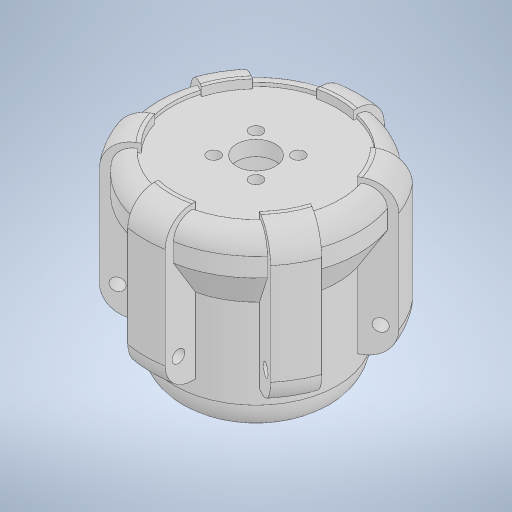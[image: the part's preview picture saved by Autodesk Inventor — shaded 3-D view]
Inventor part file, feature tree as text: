
AUTODESK INVENTOR PART (.ipt)
format: ipt  version: 2024.3 (Build 283343000, 343)  size: 502,272 bytes
history: native  units: mm
features: sketch x7, extrude x3, fillet x3, pattern_circular x3, plane x2, hole x2, projected_geometry x2, revolve x1
ambient origin geometry x8: Origin, YZ Plane, XZ Plane, XY Plane, X Axis, Y Axis, Z Axis, Center Point
bodies: Solid2 (feature_tree)
feature tree (23):
  revolve  "Revolution2"  [1 undecoded]
  plane  "Work Plane1"
  extrude  "Extrusion1"  Depth=10.0mm
  plane  "Work Plane2"
  sketch  "Sketch7"  dims[d18=3.25mm]
  fillet  "Fillet2"  Radius=55.0mm
  pattern_circular  "Circular Pattern1"  [2 undecoded]
  fillet  "Fillet3"  Radius=7.0mm
  hole  "Hole2"  [1 undecoded]
  extrude  "Extrusión3"  Depth=7.0mm
  fillet  "Empalme4"  Radius=8.0mm
  pattern_circular  "Patrón circular2"  [2 undecoded]
  extrude  "Extrusión4"  Depth=7.0mm
  hole  "Agujero3"  [1 undecoded]
  pattern_circular  "Patrón circular3"  [2 undecoded]
  sketch  "Sketch4"  dims[d11=36.85mm d12=10.4mm]
  sketch  "Sketch5"  dims[d13=5.0mm d14=10.0mm d15=55.0mm]
  sketch  "Sketch8"  dims[d19=10.0mm]
  sketch  "Boceto10"  dims[d22=43.425mm]
  projected_geometry  "Contorno proyectado2"
  sketch  "Boceto11"  dims[d24=90.0deg]
  projected_geometry  "Contorno proyectado3"
  sketch  "Boceto12"  dims[d25=-24.682mm d29=15.0mm d30=0.0mm d41=7.0mm d42=60.0mm d43=360.0deg d45=3.0mm d48=8.0mm d50=5.0mm d51=11.314mm d52=3.4mm d53=6.0mm d54=6.3mm d55=2.0mm d56=90.0deg d57=8.0mm d58=20.594885mm d59=50.0mm d63=26.0mm d64=0.0mm d65=7.0mm d66=60.0mm d67=360.0deg d69=1.0mm d70=0.0mm d72=8.0mm d73=3.4mm d74=6.0mm d75=6.3mm d76=2.0mm d77=90.0deg d78=8.0mm d79=20.594885mm d80=60.0mm d81=360.0deg d83=25.74mm d60=20.594885mm d61=0.0625mm d62=0.75mm]
note: 9 required parameter values undecoded (feature->parameter linkage not recoverable at this tier; creation-order binding heuristic only, values carry confidence <= 0.55)